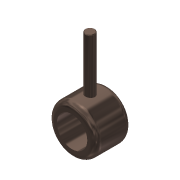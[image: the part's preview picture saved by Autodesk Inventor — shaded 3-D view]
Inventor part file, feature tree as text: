
AUTODESK INVENTOR PART (.ipt)
format: ipt  version: 2015 (Build 190159000, 159)  size: 151,040 bytes
history: native  units: mm
features: extrude x3, sketch x3, fillet x2
ambient origin geometry x8: Origin, YZ Plane, XZ Plane, XY Plane, X Axis, Y Axis, Z Axis, Center Point
bodies: Solid1 (feature_tree)
feature tree (8):
  extrude  "Extrusion1"  Depth=40.0mm
  fillet  "Fillet2"  Radius=30.0mm
  extrude  "Extrusion6"  Depth=5.0mm
  extrude  "Extrusion7"  Depth=1.0mm TaperAngle=0.0deg
  fillet  "Fillet3"  Radius=1.0mm
  sketch  "Sketch1"  dims[d0=25.4mm d1=40.0mm d6=30.0mm d7=0.0mm]
  sketch  "Sketch6"  dims[d32=5.0mm d33=8.0mm]
  sketch  "Sketch7"  dims[d34=65.4mm d35=0.0mm d36=40.0mm d37=0.0mm d47=1.0mm]
